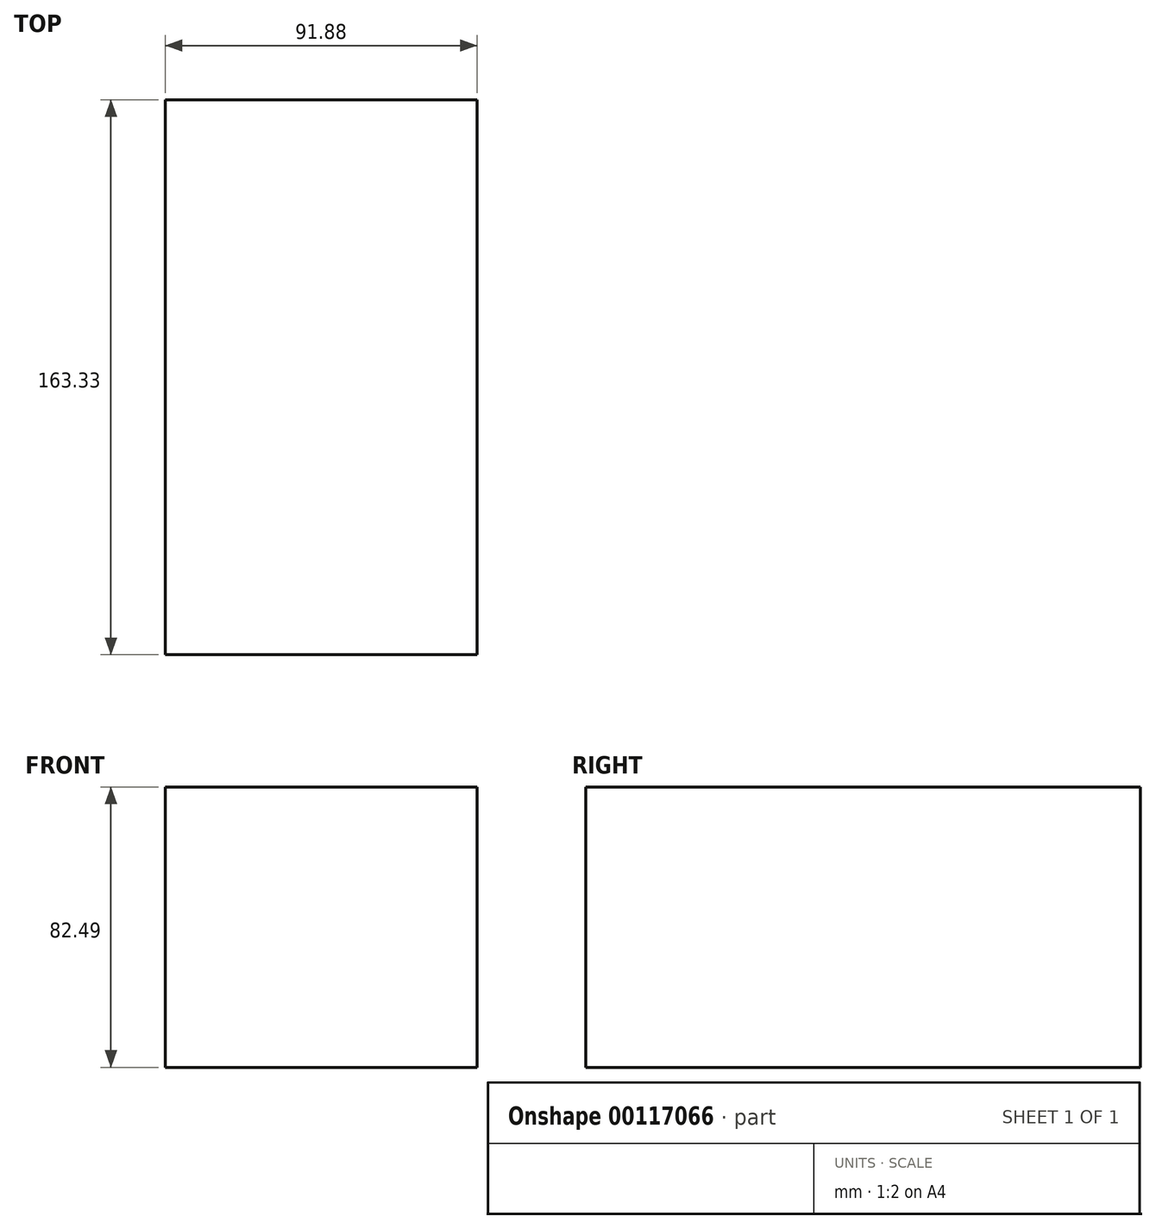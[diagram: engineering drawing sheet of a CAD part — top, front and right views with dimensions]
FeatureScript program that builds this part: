
annotation { "Feature Type Name" : "Feature", "Feature Type Description" : "" }
export const myFeature = defineFeature(function(context is Context, id is Id, definition is map)
    precondition{}
    {
        {
            var Q0;
            Q0=qCreatedBy(makeId("Front.planeOp"),FACE);
            var sketch = newSketch(context, id + "F0", { "sketchPlane" : qUnion([Q0])});
            skLineSegment(sketch, "E0.bottom", {"start": v(-42.33, 29.42) * mm, "end": v(49.55, 29.42) * mm});
            skLineSegment(sketch, "E0.top", {"start": v(-42.33, -53.07) * mm, "end": v(49.55, -53.07) * mm});
            skLineSegment(sketch, "E0.left", {"start": v(-42.33, 29.42) * mm, "end": v(-42.33, -53.07) * mm});
            skLineSegment(sketch, "E0.right", {"start": v(49.55, 29.42) * mm, "end": v(49.55, -53.07) * mm});
            skSolve(sketch);
        }
        {
            var Q0;
            Q0=makeQuery(id+"F0.imprint","IMPRINT",FACE,{"disambiguationData":[TD([[makeQuery(id+"F0.imprint","IMPRINT",EDGE,{"derivedFrom":sQuery(id+"F0.wireOp",EDGE,"E0.bottom")}),-1.0]])]});
            extrude(context, id + "F1", {"entities" : qUnion([Q0]), "depth" : 112.53 * mm});
        }
        {
            var Q0;
            Q0=qCreatedBy(makeId("Front.planeOp"),FACE);
            var sketch = newSketch(context, id + "F2", { "sketchPlane" : qUnion([Q0])});
            skCircle(sketch, "E1", {"center": v(-13.4, -3.28) * mm, "radius": 18.76 * mm});
            skSolve(sketch);
        }
        {
            var Q0;
            Q0=makeQuery(id+"F1.opExtrude","CAP_FACE",FACE,{"disambiguationData":[OSD([sQuery(id+"F0.wireOp",EDGE,"E0.bottom"),sQuery(id+"F0.wireOp",EDGE,"E0.top"),sQuery(id+"F0.wireOp",EDGE,"E0.left"),sQuery(id+"F0.wireOp",EDGE,"E0.right")])],"isStart":false});
            var Q1;
            Q1=makeQuery(id+"F2.imprint","IMPRINT",FACE,{"disambiguationData":[TD([[makeQuery(id+"F2.imprint","IMPRINT",EDGE,{"derivedFrom":sQuery(id+"F2.wireOp",EDGE,"E1")}),1.0]])]});
            var Q2;
            Q2=makeQuery(id+"F1.opExtrude","CAP_FACE",FACE,{"disambiguationData":[OSD([sQuery(id+"F0.wireOp",EDGE,"E0.bottom"),sQuery(id+"F0.wireOp",EDGE,"E0.top"),sQuery(id+"F0.wireOp",EDGE,"E0.left"),sQuery(id+"F0.wireOp",EDGE,"E0.right")])],"isStart":true});
            extrude(context, id + "F3", {"entities" : qUnion([Q0, Q1, Q2]), "operationType" : NewBodyOperationType.ADD, "depth" : 25.4 * mm});
        }
        {
            var Q0;
            {var subQ0=sQuery(id+"F0.wireOp",EDGE,"E0.right");var subQ1=sQuery(id+"F0.wireOp",EDGE,"E0.left");var subQ2=sQuery(id+"F0.wireOp",EDGE,"E0.top");var subQ3=sQuery(id+"F0.wireOp",EDGE,"E0.bottom");Q0=makeQuery(id+"F3.opExtrude","CAP_FACE",FACE,{"disambiguationData":[OSD([subQ3,subQ2,subQ1,subQ0]),TDD([makeQuery(id+"F1.opExtrude","CAP_FACE",FACE,{"disambiguationData":[OSD([subQ3,subQ2,subQ1,subQ0])],"isStart":false})])],"isStart":false});}
            var Q1;
            Q1=makeQuery(id+"F1.opExtrude","CAP_FACE",FACE,{"disambiguationData":[OSD([sQuery(id+"F0.wireOp",EDGE,"E0.bottom"),sQuery(id+"F0.wireOp",EDGE,"E0.top"),sQuery(id+"F0.wireOp",EDGE,"E0.left"),sQuery(id+"F0.wireOp",EDGE,"E0.right")])],"isStart":true});
            extrude(context, id + "F4", {"entities" : qUnion([Q0, Q1]), "operationType" : NewBodyOperationType.ADD, "depth" : 25.4 * mm});
        }
    });
